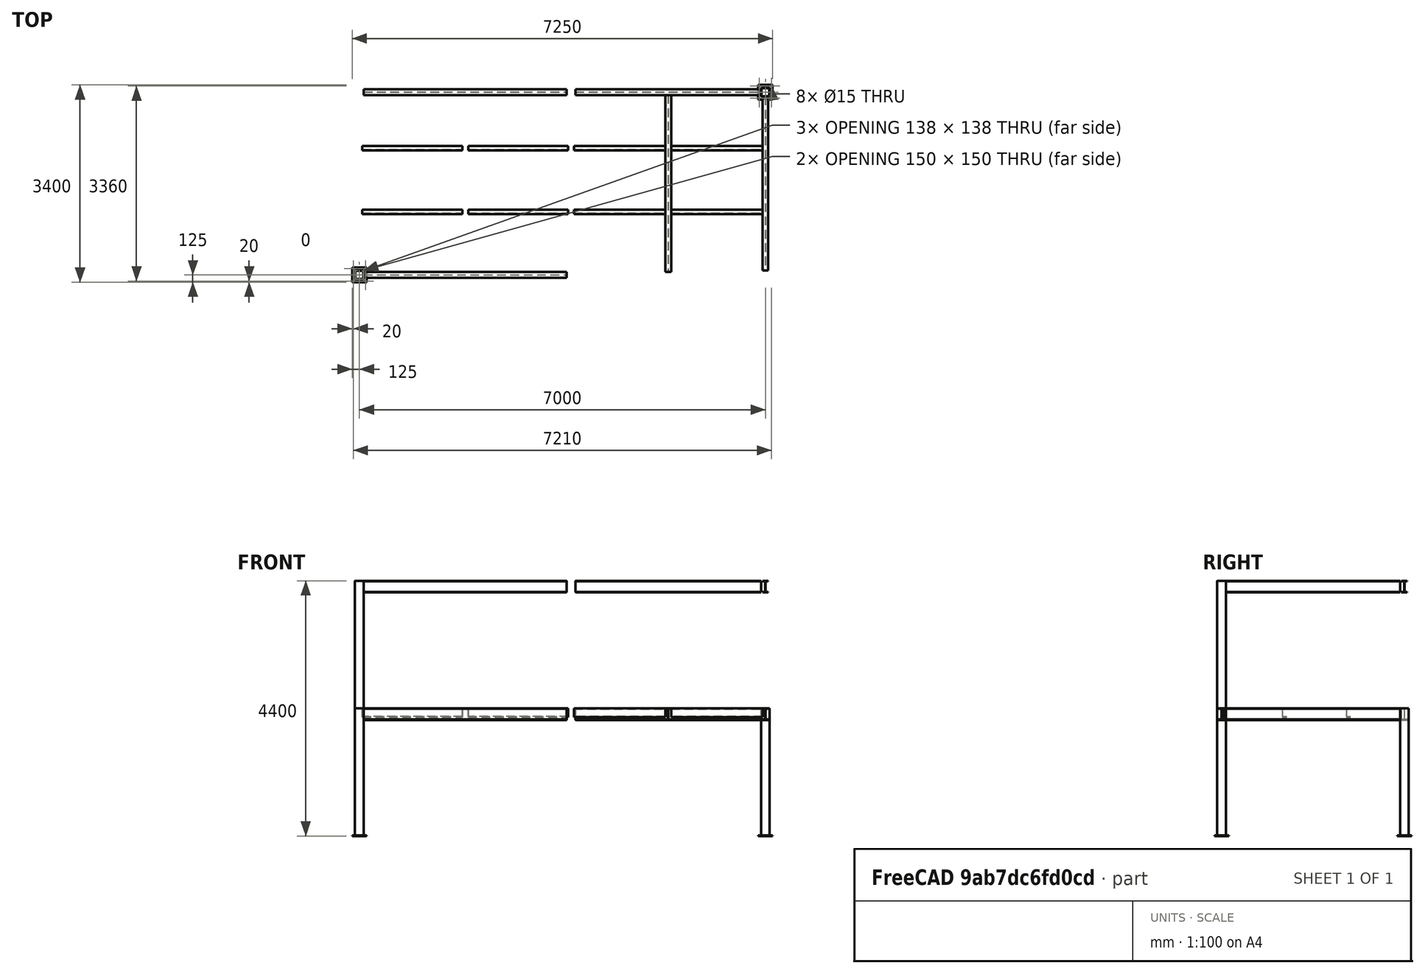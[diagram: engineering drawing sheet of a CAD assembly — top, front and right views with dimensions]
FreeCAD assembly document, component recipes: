
FREECAD ASSEMBLY — COMPONENT RECIPES ("steelframe")

This assembly document has 8 components, labeled P0..P7 below (a component is one placed body or linked part). 0 of them carry a construction recipe — the FreeCAD feature program that regenerates the part from scratch, quoted from this document or its linked companion documents; the rest are supplied as boundary geometry only. No exploded tour is included for this assembly.
COMPONENT P0 — geometry summary ("Square-steel pipe002"; no construction recipe available for this part):
  bounding box: 2200.0 x 250.0 x 250.0 mm
  tessellated surface: 596 triangles
  volume: 7925111 mm^3 (6% of its bounding box)
  symmetry: 4-fold rotationally symmetric about the z axis; mirror-symmetric across its x mid-plane, y mid-plane
COMPONENT P1 — geometry summary ("Square-steel pipe003"; no construction recipe available for this part):
  bounding box: 2200.0 x 250.0 x 250.0 mm
  tessellated surface: 596 triangles
  volume: 7925111 mm^3 (6% of its bounding box)
  symmetry: 4-fold rotationally symmetric about the z axis; mirror-symmetric across its x mid-plane, y mid-plane
COMPONENT P2 — geometry summary ("H_thin003"; no construction recipe available for this part):
  bounding box: 3500.0 x 200.0 x 100.0 mm
  tessellated surface: 140 triangles
  volume: 9505536 mm^3 (14% of its bounding box)
  symmetry: 2-fold rotationally symmetric about the x axis; 2-fold rotationally symmetric about the y axis; 2-fold rotationally symmetric about the z axis; mirror-symmetric across its x mid-plane, y mid-plane, z mid-plane
COMPONENT P3 — geometry summary ("Square-steel pipe004"; no construction recipe available for this part):
  bounding box: 2200.0 x 250.0 x 250.0 mm
  tessellated surface: 596 triangles
  volume: 7925111 mm^3 (6% of its bounding box)
  symmetry: 4-fold rotationally symmetric about the z axis; mirror-symmetric across its x mid-plane, y mid-plane
COMPONENT P4 — geometry summary ("SQ_Pipe001"; no construction recipe available for this part):
  bounding box: 2200.0 x 150.0 x 150.0 mm
  tessellated surface: 208 triangles
  volume: 7399242 mm^3 (15% of its bounding box)
  symmetry: 2-fold rotationally symmetric about the x axis; 2-fold rotationally symmetric about the y axis; 4-fold rotationally symmetric about the z axis; mirror-symmetric across its x mid-plane, y mid-plane, z mid-plane
COMPONENT P5 — geometry summary ("SQ_Pipe005"; no construction recipe available for this part):
  bounding box: 2200.0 x 150.0 x 150.0 mm
  tessellated surface: 208 triangles
  volume: 7399242 mm^3 (15% of its bounding box)
  symmetry: 2-fold rotationally symmetric about the x axis; 2-fold rotationally symmetric about the y axis; 4-fold rotationally symmetric about the z axis; mirror-symmetric across its x mid-plane, y mid-plane, z mid-plane
COMPONENT P6 — geometry summary ("H_thin009"; no construction recipe available for this part):
  bounding box: 3500.0 x 200.0 x 100.0 mm
  tessellated surface: 140 triangles
  volume: 9505536 mm^3 (14% of its bounding box)
  symmetry: 2-fold rotationally symmetric about the x axis; 2-fold rotationally symmetric about the y axis; 2-fold rotationally symmetric about the z axis; mirror-symmetric across its x mid-plane, y mid-plane, z mid-plane
COMPONENT P7 — geometry summary ("H_thin010"; no construction recipe available for this part):
  bounding box: 3000.0 x 200.0 x 100.0 mm
  tessellated surface: 140 triangles
  volume: 8147602 mm^3 (14% of its bounding box)
  symmetry: 2-fold rotationally symmetric about the x axis; 2-fold rotationally symmetric about the y axis; 2-fold rotationally symmetric about the z axis; mirror-symmetric across its x mid-plane, y mid-plane, z mid-plane
PROVENANCE & LICENSES
A FreeCAD (.FCStd) document from a public repository crawl; recipes are the document's own serialized feature recipes (and, for linked parts, companion documents' recipes).
License: as declared in the source repository (recorded in the dataset sidecar).
